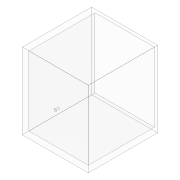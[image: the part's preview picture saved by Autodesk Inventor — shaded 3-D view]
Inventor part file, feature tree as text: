
AUTODESK INVENTOR PART (.ipt)
format: ipt  version: 2020 (Build 240168000, 168)  size: 112,128 bytes
history: native  units: mm
features: sketch x3, extrude x2, hole x1, fillet x1
ambient origin geometry x8: Origin, YZ Plane, XZ Plane, XY Plane, X Axis, Y Axis, Z Axis, Center Point
bodies: Volumenkörper1 (feature_tree)
feature tree (7):
  extrude  "Extrusion1"  Depth=5.0mm
  extrude  "Extrusion2"  Depth=5.0mm
  hole  "Bohrung1"  [1 undecoded]
  fillet  "Rundung1"  Radius=100.0mm
  sketch  "Skizze1"  dims[d0=5.0mm d1=5.0mm]
  sketch  "Skizze2"  dims[d2=5.0mm d3=5.0mm]
  sketch  "Skizze3"  dims[d4=90.0mm d5=105.0mm d6=100.0mm d7=0.0mm d8=5.0mm d9=0.0mm d10=50.0mm d11=57.5mm d12=3.0mm d13=6.0mm d14=4.0mm d15=2.0mm d16=90.0deg d17=8.0mm d18=20.594885mm d19=0.4mm]
note: 1 required parameter value undecoded (feature->parameter linkage not recoverable at this tier; creation-order binding heuristic only, values carry confidence <= 0.55)
